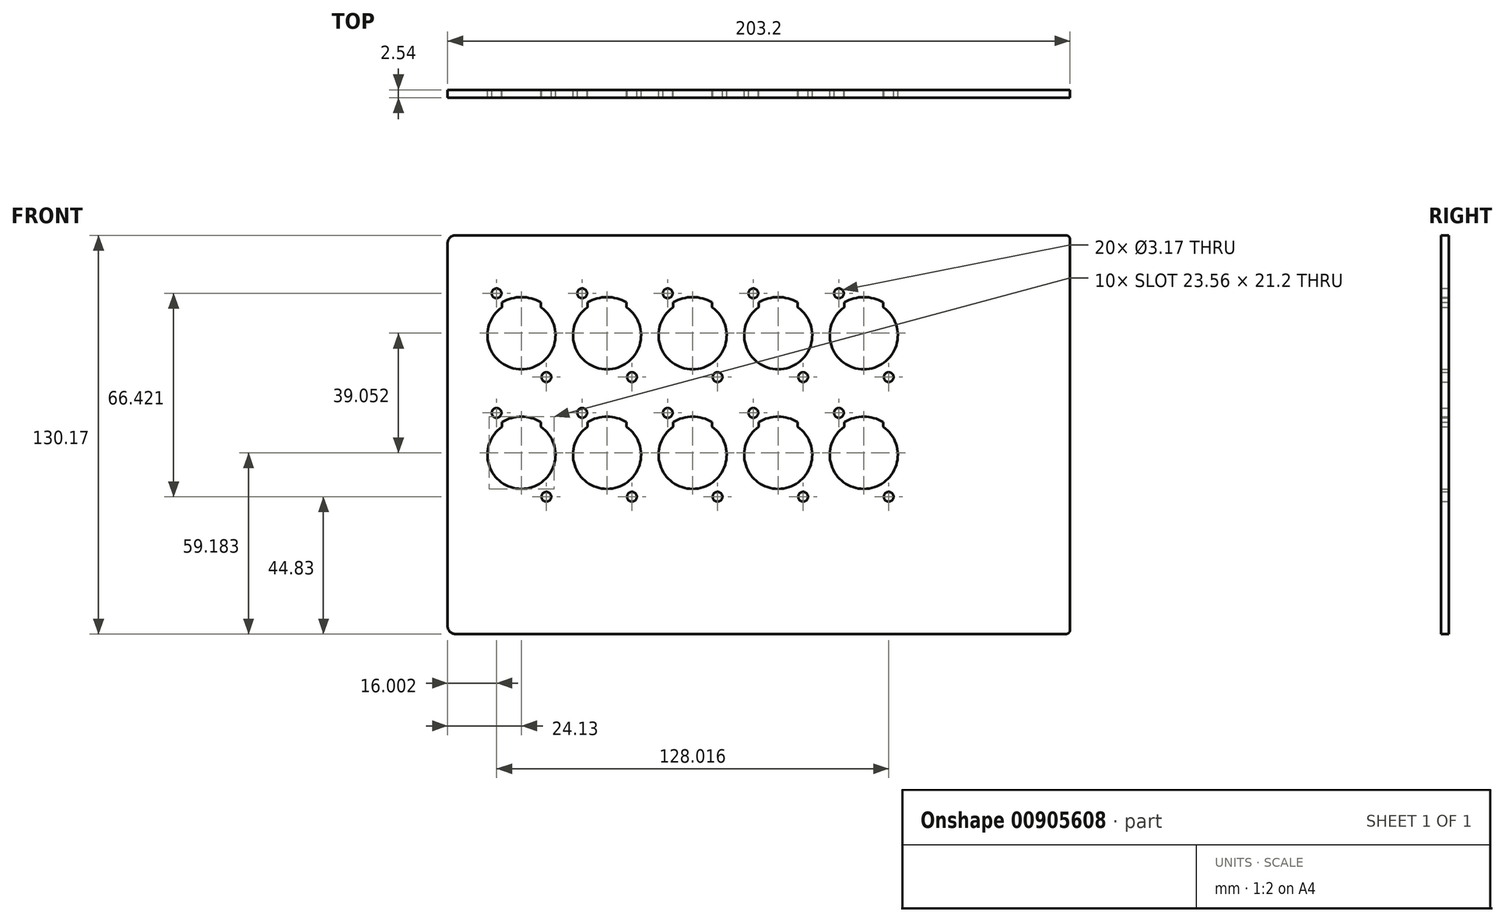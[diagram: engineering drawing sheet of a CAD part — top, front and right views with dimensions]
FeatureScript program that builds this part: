
annotation { "Feature Type Name" : "Feature", "Feature Type Description" : "" }
export const myFeature = defineFeature(function(context is Context, id is Id, definition is map)
    precondition{}
    {
        {
            var Q0;
            Q0=qCreatedBy(makeId("Front.planeOp"),FACE);
            var sketch = newSketch(context, id + "F0", { "sketchPlane" : qUnion([Q0])});
            skArc(sketch, "E0", {"start": v(-90.17, 28.65) * mm, "mid": v(-83.82, 8.41) * mm, "end": v(-77.47, 28.65) * mm});
            skPoint(sketch, "E0.centerSnap0", {"position": v(-71.12, 19.53) * mm});
            skPoint(sketch, "E0.centerSnap1", {"position": v(-83.82, 37.78) * mm});
            skCircle(sketch, "E1", {"center": v(-91.95, 33.21) * mm, "radius": 1.59 * mm});
            skCircle(sketch, "E2", {"center": v(-75.7, 5.84) * mm, "radius": 1.59 * mm});
            skArc(sketch, "E3", {"start": v(-77.47, 30.24) * mm, "mid": v(-83.82, 31.98) * mm, "end": v(-90.17, 30.24) * mm});
            skLineSegment(sketch, "E4", {"start": v(-90.17, 30.24) * mm, "end": v(-90.17, 28.65) * mm});
            skLineSegment(sketch, "E5", {"start": v(-77.47, 30.24) * mm, "end": v(-77.47, 28.65) * mm});
            skArc(sketch, "E6", {"start": v(-62.23, 28.65) * mm, "mid": v(-55.88, 8.41) * mm, "end": v(-49.53, 28.65) * mm});
            skPoint(sketch, "E6.centerSnap0", {"position": v(-43.18, 19.53) * mm});
            skPoint(sketch, "E6.centerSnap1", {"position": v(-55.88, 37.78) * mm});
            skCircle(sketch, "E7", {"center": v(-64, 33.21) * mm, "radius": 1.59 * mm});
            skCircle(sketch, "E8", {"center": v(-47.75, 5.84) * mm, "radius": 1.59 * mm});
            skArc(sketch, "E9", {"start": v(-49.53, 30.24) * mm, "mid": v(-55.88, 31.98) * mm, "end": v(-62.23, 30.24) * mm});
            skLineSegment(sketch, "E10", {"start": v(-62.23, 30.24) * mm, "end": v(-62.23, 28.65) * mm});
            skLineSegment(sketch, "E11", {"start": v(-49.53, 30.24) * mm, "end": v(-49.53, 28.65) * mm});
            skArc(sketch, "E12", {"start": v(-34.3, 28.65) * mm, "mid": v(-27.94, 8.41) * mm, "end": v(-21.59, 28.65) * mm});
            skPoint(sketch, "E12.centerSnap0", {"position": v(-15.24, 19.53) * mm});
            skPoint(sketch, "E12.centerSnap1", {"position": v(-27.94, 37.78) * mm});
            skCircle(sketch, "E13", {"center": v(-36.07, 33.21) * mm, "radius": 1.59 * mm});
            skCircle(sketch, "E14", {"center": v(-19.81, 5.84) * mm, "radius": 1.59 * mm});
            skArc(sketch, "E15", {"start": v(-21.59, 30.24) * mm, "mid": v(-27.94, 31.98) * mm, "end": v(-34.3, 30.24) * mm});
            skLineSegment(sketch, "E16", {"start": v(-34.3, 30.24) * mm, "end": v(-34.3, 28.65) * mm});
            skLineSegment(sketch, "E17", {"start": v(-21.6, 30.24) * mm, "end": v(-21.6, 28.65) * mm});
            skArc(sketch, "E18", {"start": v(-6.35, 28.65) * mm, "mid": v(0, 8.41) * mm, "end": v(6.35, 28.65) * mm});
            skPoint(sketch, "E18.centerSnap0", {"position": v(12.7, 19.53) * mm});
            skPoint(sketch, "E18.centerSnap1", {"position": v(0, 37.78) * mm});
            skCircle(sketch, "E19", {"center": v(-8.13, 33.21) * mm, "radius": 1.59 * mm});
            skCircle(sketch, "E20", {"center": v(8.13, 5.84) * mm, "radius": 1.59 * mm});
            skArc(sketch, "E21", {"start": v(6.35, 30.24) * mm, "mid": v(0, 31.98) * mm, "end": v(-6.35, 30.24) * mm});
            skLineSegment(sketch, "E22", {"start": v(-6.35, 30.24) * mm, "end": v(-6.35, 28.65) * mm});
            skLineSegment(sketch, "E23", {"start": v(6.35, 30.24) * mm, "end": v(6.35, 28.65) * mm});
            skArc(sketch, "E24", {"start": v(21.6, 28.65) * mm, "mid": v(27.94, 8.41) * mm, "end": v(34.3, 28.65) * mm});
            skPoint(sketch, "E24.centerSnap0", {"position": v(40.64, 19.53) * mm});
            skPoint(sketch, "E24.centerSnap1", {"position": v(27.94, 37.78) * mm});
            skCircle(sketch, "E25", {"center": v(19.81, 33.21) * mm, "radius": 1.59 * mm});
            skCircle(sketch, "E26", {"center": v(36.07, 5.84) * mm, "radius": 1.59 * mm});
            skArc(sketch, "E27", {"start": v(34.3, 30.24) * mm, "mid": v(27.94, 31.98) * mm, "end": v(21.6, 30.24) * mm});
            skLineSegment(sketch, "E28", {"start": v(21.6, 30.24) * mm, "end": v(21.6, 28.65) * mm});
            skLineSegment(sketch, "E29", {"start": v(34.3, 30.24) * mm, "end": v(34.3, 28.65) * mm});
            skArc(sketch, "E30", {"start": v(-90.17, -10.4) * mm, "mid": v(-83.82, -30.64) * mm, "end": v(-77.47, -10.4) * mm});
            skPoint(sketch, "E30.centerSnap0", {"position": v(-71.12, -19.53) * mm});
            skPoint(sketch, "E30.centerSnap1", {"position": v(-83.82, -1.27) * mm});
            skCircle(sketch, "E31", {"center": v(-91.95, -5.84) * mm, "radius": 1.59 * mm});
            skCircle(sketch, "E32", {"center": v(-75.7, -33.21) * mm, "radius": 1.59 * mm});
            skArc(sketch, "E33", {"start": v(-77.47, -8.82) * mm, "mid": v(-83.82, -7.08) * mm, "end": v(-90.17, -8.82) * mm});
            skLineSegment(sketch, "E34", {"start": v(-90.17, -8.82) * mm, "end": v(-90.17, -10.4) * mm});
            skLineSegment(sketch, "E35", {"start": v(-77.47, -8.82) * mm, "end": v(-77.47, -10.4) * mm});
            skArc(sketch, "E36", {"start": v(-62.23, -10.4) * mm, "mid": v(-55.88, -30.64) * mm, "end": v(-49.53, -10.4) * mm});
            skPoint(sketch, "E36.centerSnap0", {"position": v(-43.18, -19.53) * mm});
            skPoint(sketch, "E36.centerSnap1", {"position": v(-55.88, -1.27) * mm});
            skCircle(sketch, "E37", {"center": v(-64, -5.84) * mm, "radius": 1.59 * mm});
            skCircle(sketch, "E38", {"center": v(-47.75, -33.21) * mm, "radius": 1.59 * mm});
            skArc(sketch, "E39", {"start": v(-49.53, -8.82) * mm, "mid": v(-55.88, -7.08) * mm, "end": v(-62.23, -8.82) * mm});
            skLineSegment(sketch, "E40", {"start": v(-62.23, -8.82) * mm, "end": v(-62.23, -10.4) * mm});
            skLineSegment(sketch, "E41", {"start": v(-49.53, -8.82) * mm, "end": v(-49.53, -10.4) * mm});
            skArc(sketch, "E42", {"start": v(-34.3, -10.4) * mm, "mid": v(-27.94, -30.64) * mm, "end": v(-21.6, -10.4) * mm});
            skPoint(sketch, "E42.centerSnap0", {"position": v(-15.24, -19.53) * mm});
            skPoint(sketch, "E42.centerSnap1", {"position": v(-27.94, -1.27) * mm});
            skCircle(sketch, "E43", {"center": v(-36.07, -5.84) * mm, "radius": 1.59 * mm});
            skCircle(sketch, "E44", {"center": v(-19.81, -33.21) * mm, "radius": 1.59 * mm});
            skArc(sketch, "E45", {"start": v(-21.6, -8.82) * mm, "mid": v(-27.94, -7.08) * mm, "end": v(-34.3, -8.82) * mm});
            skLineSegment(sketch, "E46", {"start": v(-34.3, -8.82) * mm, "end": v(-34.3, -10.4) * mm});
            skLineSegment(sketch, "E47", {"start": v(-21.6, -8.82) * mm, "end": v(-21.59, -10.4) * mm});
            skArc(sketch, "E48", {"start": v(-6.35, -10.4) * mm, "mid": v(0, -30.64) * mm, "end": v(6.35, -10.4) * mm});
            skPoint(sketch, "E48.centerSnap0", {"position": v(12.7, -19.53) * mm});
            skPoint(sketch, "E48.centerSnap1", {"position": v(0, -1.27) * mm});
            skCircle(sketch, "E49", {"center": v(-8.13, -5.84) * mm, "radius": 1.59 * mm});
            skCircle(sketch, "E50", {"center": v(8.13, -33.21) * mm, "radius": 1.59 * mm});
            skArc(sketch, "E51", {"start": v(6.35, -8.82) * mm, "mid": v(0, -7.08) * mm, "end": v(-6.35, -8.82) * mm});
            skLineSegment(sketch, "E52", {"start": v(-6.35, -8.82) * mm, "end": v(-6.35, -10.4) * mm});
            skLineSegment(sketch, "E53", {"start": v(6.35, -8.82) * mm, "end": v(6.35, -10.4) * mm});
            skArc(sketch, "E54", {"start": v(21.6, -10.4) * mm, "mid": v(27.94, -30.64) * mm, "end": v(34.3, -10.4) * mm});
            skPoint(sketch, "E54.centerSnap0", {"position": v(40.64, -19.53) * mm});
            skPoint(sketch, "E54.centerSnap1", {"position": v(27.94, -1.27) * mm});
            skCircle(sketch, "E55", {"center": v(19.81, -5.84) * mm, "radius": 1.59 * mm});
            skCircle(sketch, "E56", {"center": v(36.07, -33.21) * mm, "radius": 1.59 * mm});
            skArc(sketch, "E57", {"start": v(34.3, -8.82) * mm, "mid": v(27.94, -7.08) * mm, "end": v(21.6, -8.82) * mm});
            skLineSegment(sketch, "E58", {"start": v(21.6, -8.82) * mm, "end": v(21.6, -10.4) * mm});
            skLineSegment(sketch, "E59", {"start": v(34.3, -8.82) * mm, "end": v(34.3, -10.4) * mm});
            skLineSegment(sketch, "E60.bottom", {"start": v(-105.4, 52.13) * mm, "end": v(93.98, 52.13) * mm});
            skLineSegment(sketch, "E60.top", {"start": v(-105.4, -78.04) * mm, "end": v(93.98, -78.04) * mm});
            skLineSegment(sketch, "E60.left", {"start": v(-107.95, 49.6) * mm, "end": v(-107.95, -75.5) * mm});
            skLineSegment(sketch, "E60.right", {"start": v(95.25, 50.86) * mm, "end": v(95.25, -76.77) * mm});
            skArc(sketch, "E61", {"start": v(-105.4, 52.13) * mm, "mid": v(-107.2, 51.4) * mm, "end": v(-107.95, 49.6) * mm});
            skPoint(sketch, "E62.orphan", {"position": v(-107.95, 52.13) * mm});
            skArc(sketch, "E63", {"start": v(95.25, 50.86) * mm, "mid": v(94.88, 51.76) * mm, "end": v(93.98, 52.13) * mm});
            skArc(sketch, "E64", {"start": v(93.98, -78.04) * mm, "mid": v(94.88, -77.67) * mm, "end": v(95.25, -76.77) * mm});
            skArc(sketch, "E65", {"start": v(-107.95, -75.5) * mm, "mid": v(-107.2, -77.3) * mm, "end": v(-105.4, -78.04) * mm});
            skSolve(sketch);
        }
        {
            var Q0;
            Q0=makeQuery(id+"F0.imprint","IMPRINT",FACE,{"disambiguationData":[TD([[makeQuery(id+"F0.imprint","IMPRINT",EDGE,{"derivedFrom":sQuery(id+"F0.wireOp",EDGE,"E0")}),-1.0]])]});
            extrude(context, id + "F1", {"entities" : qUnion([Q0]), "depth" : 2.54 * mm, "offsetDistance" : 25.4 * mm});
        }
    });
